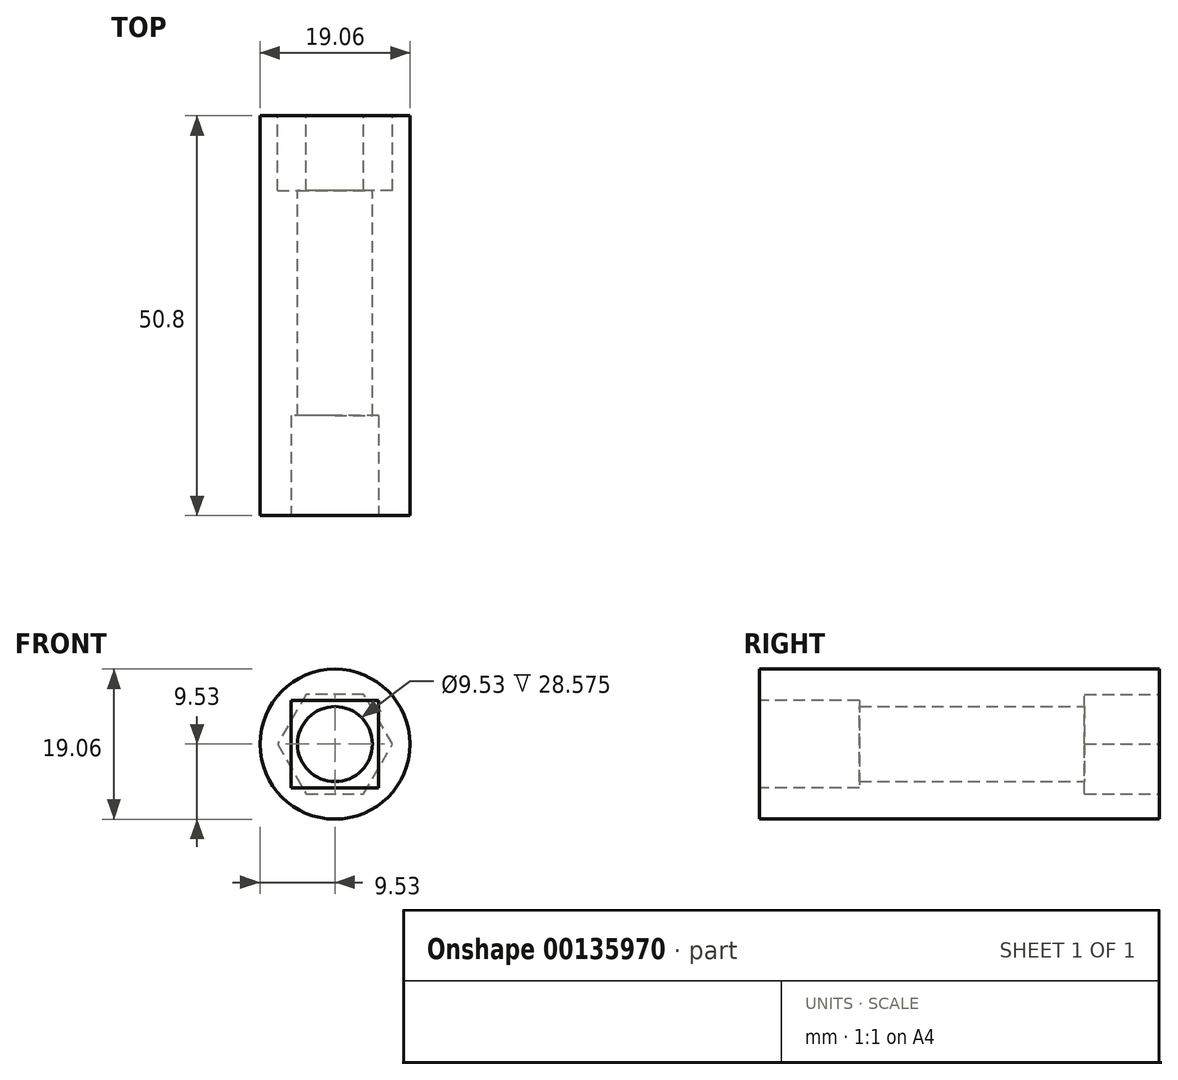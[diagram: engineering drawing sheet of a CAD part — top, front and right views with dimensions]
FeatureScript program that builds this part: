
annotation { "Feature Type Name" : "Feature", "Feature Type Description" : "" }
export const myFeature = defineFeature(function(context is Context, id is Id, definition is map)
    precondition{}
    {
        {
            var Q0;
            Q0=qCreatedBy(makeId("Front.planeOp"),FACE);
            var sketch = newSketch(context, id + "F0", { "sketchPlane" : qUnion([Q0])});
            skCircle(sketch, "E0", {"center": v(0, 0) * mm, "radius": 9.53 * mm});
            skSolve(sketch);
        }
        {
            var Q0;
            Q0 = qSketchRegion(id + "F0", true);
            extrude(context, id + "F1", {"entities" : qUnion([Q0]), "depth" : 25.4 * mm});
        }
        {
            var Q0;
            Q0=makeQuery(id+"F1.opExtrude","CAP_FACE",FACE,{"disambiguationData":[OSD([sQuery(id+"F0.wireOp",EDGE,"E0")])],"isStart":false});
            extrude(context, id + "F2", {"entities" : qUnion([Q0]), "operationType" : NewBodyOperationType.ADD, "depth" : 25.4 * mm});
        }
        {
            var Q0;
            Q0=qCreatedBy(makeId("Front.planeOp"),FACE);
            var sketch = newSketch(context, id + "F3", { "sketchPlane" : qUnion([Q0])});
            skLineSegment(sketch, "E1.bottom", {"start": v(4.76, 4.76) * mm, "end": v(-4.76, 4.76) * mm});
            skLineSegment(sketch, "E1.top", {"start": v(4.76, -4.76) * mm, "end": v(-4.76, -4.76) * mm});
            skLineSegment(sketch, "E1.left", {"start": v(4.76, 4.76) * mm, "end": v(4.76, -4.76) * mm});
            skLineSegment(sketch, "E1.right", {"start": v(-4.76, 4.76) * mm, "end": v(-4.76, -4.76) * mm});
            skPoint(sketch, "E1.middle", {"position": v(0, 0) * mm});
            skCircle(sketch, "E2", {"center": v(0, 0) * mm, "radius": 4.76 * mm});
            skSolve(sketch);
        }
        {
            var Q0;
            {var subQ0=sQuery(id+"F3.wireOp",EDGE,"E2");var subQ1=makeQuery(id+"F3.imprint","INTERSECT",VERTEX,{"derivedFrom":[sQuery(id+"F3.wireOp",EDGE,"E1.bottom"),subQ0]});Q0=makeQuery(id+"F3.imprint","IMPRINT",FACE,{"disambiguationData":[TD([[makeQuery(id+"F3.imprint","IMPRINT",EDGE,{"disambiguationData":[TD([[subQ1,1.0]])],"derivedFrom":subQ0}),1.0]])]});}
            extrude(context, id + "F4", {"entities" : qUnion([Q0]), "operationType" : NewBodyOperationType.REMOVE, "endBound" : BoundingType.THROUGH_ALL, "depth" : 25.4 * mm});
        }
        {
            var Q0;
            Q0=makeQuery(id+"F1.opExtrude","CAP_FACE",FACE,{"disambiguationData":[OSD([sQuery(id+"F0.wireOp",EDGE,"E0")])],"isStart":true});
            var sketch = newSketch(context, id + "F5", { "sketchPlane" : qUnion([Q0])});
            skCircle(sketch, "E3.cCircle", {"center": v(0, 0) * mm, "radius": 6.32 * mm, "construction": true});
            skLineSegment(sketch, "E3.0", {"start": v(-3.65, 6.32) * mm, "end": v(3.65, 6.32) * mm});
            skLineSegment(sketch, "E3.1", {"start": v(3.65, 6.32) * mm, "end": v(7.3, 0) * mm});
            skLineSegment(sketch, "E3.2", {"start": v(7.3, 0) * mm, "end": v(3.65, -6.32) * mm});
            skLineSegment(sketch, "E3.3", {"start": v(3.65, -6.32) * mm, "end": v(-3.65, -6.32) * mm});
            skLineSegment(sketch, "E3.4", {"start": v(-3.65, -6.32) * mm, "end": v(-7.3, 0) * mm});
            skLineSegment(sketch, "E3.5", {"start": v(-7.3, 0) * mm, "end": v(-3.65, 6.32) * mm});
            skPoint(sketch, "E3.0.midPoint", {"position": v(0, 6.32) * mm});
            skSolve(sketch);
        }
        {
            var Q0;
            Q0 = qSketchRegion(id + "F5", true);
            extrude(context, id + "F6", {"entities" : qUnion([Q0]), "operationType" : NewBodyOperationType.REMOVE, "oppositeDirection" : true, "depth" : 9.52 * mm});
        }
        {
            var Q0;
            Q0=makeQuery(id+"F2.opExtrude","CAP_FACE",FACE,{"disambiguationData":[OSD([sQuery(id+"F0.wireOp",EDGE,"E0")])],"isStart":false});
            var sketch = newSketch(context, id + "F7", { "sketchPlane" : qUnion([Q0])});
            skLineSegment(sketch, "E4.bottom", {"start": v(5.55, 5.55) * mm, "end": v(-5.55, 5.55) * mm});
            skLineSegment(sketch, "E4.top", {"start": v(5.55, -5.55) * mm, "end": v(-5.55, -5.55) * mm});
            skLineSegment(sketch, "E4.left", {"start": v(5.55, 5.55) * mm, "end": v(5.55, -5.55) * mm});
            skLineSegment(sketch, "E4.right", {"start": v(-5.55, 5.55) * mm, "end": v(-5.55, -5.55) * mm});
            skPoint(sketch, "E4.middle", {"position": v(0, 0) * mm});
            skSolve(sketch);
        }
        {
            var Q0;
            Q0 = qSketchRegion(id + "F7", true);
            extrude(context, id + "F8", {"entities" : qUnion([Q0]), "operationType" : NewBodyOperationType.REMOVE, "oppositeDirection" : true, "depth" : 12.7 * mm});
        }
    });
